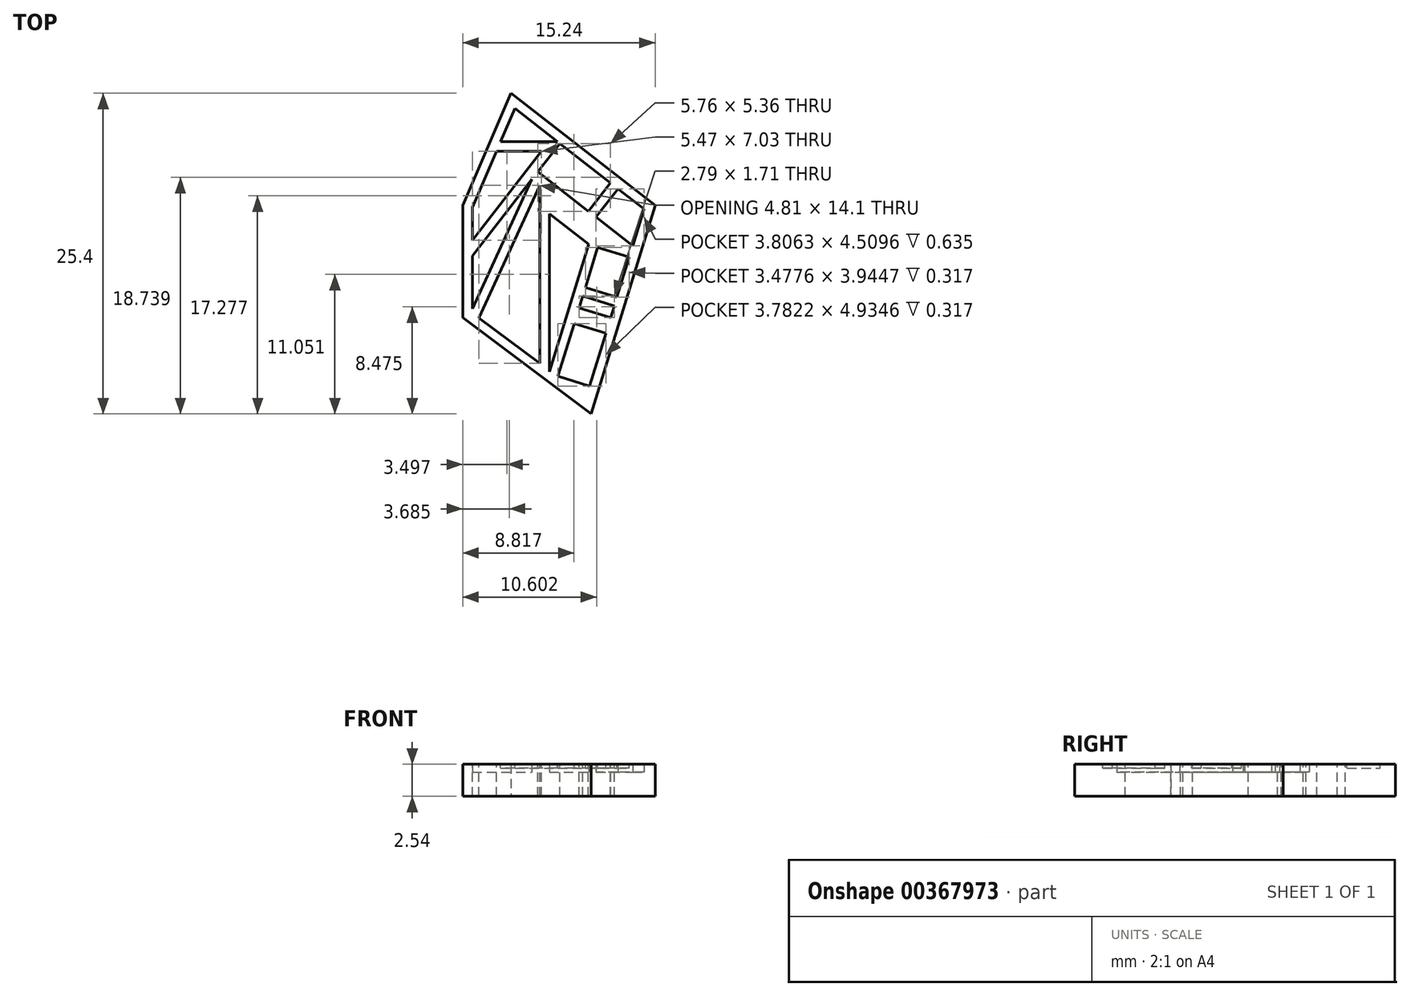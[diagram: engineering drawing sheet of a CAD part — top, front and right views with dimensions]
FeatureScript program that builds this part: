
annotation { "Feature Type Name" : "Feature", "Feature Type Description" : "" }
export const myFeature = defineFeature(function(context is Context, id is Id, definition is map)
    precondition{}
    {
        {
            var Q0;
            Q0=qCreatedBy(makeId("Top.planeOp"),FACE);
            var sketch = newSketch(context, id + "F0", { "sketchPlane" : qUnion([Q0])});
            skLineSegment(sketch, "E0", {"start": v(0, 17.78) * mm, "end": v(11.43, 8.9) * mm});
            skLineSegment(sketch, "E1", {"start": v(11.43, 8.9) * mm, "end": v(6.35, -7.62) * mm});
            skLineSegment(sketch, "E2", {"start": v(6.35, -7.62) * mm, "end": v(-3.81, 0) * mm});
            skLineSegment(sketch, "E3", {"start": v(-3.8, 0) * mm, "end": v(-3.8, 8.9) * mm});
            skLineSegment(sketch, "E4", {"start": v(-3.81, 8.9) * mm, "end": v(0, 17.78) * mm});
            skSolve(sketch);
        }
        {
            var Q0;
            Q0=makeQuery(id+"F0.imprint","IMPRINT",FACE,{"disambiguationData":[TD([[makeQuery(id+"F0.imprint","IMPRINT",EDGE,{"derivedFrom":sQuery(id+"F0.wireOp",EDGE,"E0")}),-1.0]])]});
            extrude(context, id + "F1", {"entities" : qUnion([Q0]), "depth" : 2.54 * mm});
        }
        {
            var Q0;
            Q0=makeQuery(id+"F1.opExtrude","CAP_FACE",FACE,{"disambiguationData":[OSD([sQuery(id+"F0.wireOp",EDGE,"E0"),sQuery(id+"F0.wireOp",EDGE,"E1"),sQuery(id+"F0.wireOp",EDGE,"E2"),sQuery(id+"F0.wireOp",EDGE,"E3"),sQuery(id+"F0.wireOp",EDGE,"E4")])],"isStart":false});
            var sketch = newSketch(context, id + "F2", { "sketchPlane" : qUnion([Q0])});
            skLineSegment(sketch, "E5", {"start": v(0.31, 16.57) * mm, "end": v(-0.82, 13.93) * mm});
            skLineSegment(sketch, "E6", {"start": v(-0.82, 13.93) * mm, "end": v(3.7, 13.93) * mm});
            skLineSegment(sketch, "E7", {"start": v(3.7, 13.93) * mm, "end": v(0.31, 16.57) * mm});
            skLineSegment(sketch, "E8", {"start": v(2.42, 13.17) * mm, "end": v(-1.15, 13.17) * mm});
            skLineSegment(sketch, "E9", {"start": v(-1.15, 13.17) * mm, "end": v(-3.05, 8.73) * mm});
            skLineSegment(sketch, "E10", {"start": v(-3.05, 8.73) * mm, "end": v(-3.05, 6.14) * mm});
            skLineSegment(sketch, "E11", {"start": v(-3.05, 6.14) * mm, "end": v(2.42, 13.17) * mm});
            skLineSegment(sketch, "E12", {"start": v(3.88, 13.8) * mm, "end": v(2.13, 11.56) * mm});
            skLineSegment(sketch, "E13", {"start": v(2.13, 11.56) * mm, "end": v(6.14, 8.44) * mm});
            skLineSegment(sketch, "E14", {"start": v(6.14, 8.44) * mm, "end": v(7.89, 10.68) * mm});
            skLineSegment(sketch, "E15", {"start": v(7.89, 10.68) * mm, "end": v(3.88, 13.8) * mm});
            skLineSegment(sketch, "E16", {"start": v(8.49, 10.21) * mm, "end": v(6.74, 7.97) * mm});
            skLineSegment(sketch, "E17", {"start": v(6.74, 7.97) * mm, "end": v(9.65, 5.7) * mm});
            skLineSegment(sketch, "E18", {"start": v(9.65, 5.7) * mm, "end": v(10.55, 8.61) * mm});
            skLineSegment(sketch, "E19", {"start": v(10.55, 8.61) * mm, "end": v(8.49, 10.21) * mm});
            skLineSegment(sketch, "E20", {"start": v(1.66, 10.95) * mm, "end": v(-3.05, 4.9) * mm});
            skLineSegment(sketch, "E21", {"start": v(-3.05, 4.9) * mm, "end": v(-3.05, 0.7) * mm});
            skLineSegment(sketch, "E22", {"start": v(-3.05, 0.7) * mm, "end": v(1.66, 10.95) * mm});
            skLineSegment(sketch, "E23", {"start": v(2.28, 10.48) * mm, "end": v(2.28, -3.62) * mm});
            skLineSegment(sketch, "E24", {"start": v(2.28, -3.62) * mm, "end": v(-2.53, 0) * mm});
            skLineSegment(sketch, "E25", {"start": v(-2.53, 0) * mm, "end": v(2.28, 10.48) * mm});
            skLineSegment(sketch, "E26", {"start": v(3.04, 8.25) * mm, "end": v(3.04, -4.29) * mm});
            skLineSegment(sketch, "E27", {"start": v(3.04, -4.29) * mm, "end": v(6.16, 5.83) * mm});
            skLineSegment(sketch, "E28", {"start": v(3.04, 8.25) * mm, "end": v(6.16, 5.83) * mm});
            skLineSegment(sketch, "E29", {"start": v(6.88, 5.58) * mm, "end": v(5.9, 2.4) * mm});
            skLineSegment(sketch, "E30", {"start": v(5.9, 2.4) * mm, "end": v(8.4, 1.63) * mm});
            skLineSegment(sketch, "E31", {"start": v(8.4, 1.63) * mm, "end": v(9.38, 4.8) * mm});
            skLineSegment(sketch, "E32", {"start": v(9.38, 4.8) * mm, "end": v(6.88, 5.58) * mm});
            skLineSegment(sketch, "E33", {"start": v(5.69, 1.71) * mm, "end": v(5.4, 0.77) * mm});
            skPoint(sketch, "E33.endSnap0", {"position": v(4.6, 0.77) * mm});
            skLineSegment(sketch, "E34", {"start": v(5.4, 0.77) * mm, "end": v(7.9, 0) * mm});
            skLineSegment(sketch, "E35", {"start": v(7.9, 0) * mm, "end": v(8.19, 0.94) * mm});
            skLineSegment(sketch, "E36", {"start": v(5.69, 1.71) * mm, "end": v(8.19, 0.94) * mm});
            skLineSegment(sketch, "E37", {"start": v(5.02, -0.47) * mm, "end": v(3.73, -4.64) * mm});
            skLineSegment(sketch, "E38", {"start": v(3.73, -4.64) * mm, "end": v(6.23, -5.4) * mm});
            skLineSegment(sketch, "E39", {"start": v(6.23, -5.4) * mm, "end": v(7.52, -1.24) * mm});
            skLineSegment(sketch, "E40", {"start": v(7.52, -1.24) * mm, "end": v(5.02, -0.47) * mm});
            skSolve(sketch);
        }
        {
            var Q0;
            Q0=makeQuery(id+"F2.imprint","IMPRINT",FACE,{"disambiguationData":[TD([[makeQuery(id+"F2.imprint","IMPRINT",EDGE,{"derivedFrom":sQuery(id+"F2.wireOp",EDGE,"E8")}),1.0]])]});
            var Q1;
            Q1=makeQuery(id+"F2.imprint","IMPRINT",FACE,{"disambiguationData":[TD([[makeQuery(id+"F2.imprint","IMPRINT",EDGE,{"derivedFrom":sQuery(id+"F2.wireOp",EDGE,"E12")}),1.0]])]});
            var Q2;
            Q2=makeQuery(id+"F2.imprint","IMPRINT",FACE,{"disambiguationData":[TD([[makeQuery(id+"F2.imprint","IMPRINT",EDGE,{"derivedFrom":sQuery(id+"F2.wireOp",EDGE,"E23")}),-1.0]])]});
            var Q3;
            Q3=makeQuery(id+"F2.imprint","IMPRINT",FACE,{"disambiguationData":[TD([[makeQuery(id+"F2.imprint","IMPRINT",EDGE,{"derivedFrom":sQuery(id+"F2.wireOp",EDGE,"E33")}),1.0]])]});
            extrude(context, id + "F3", {"entities" : qUnion([Q0, Q1, Q2, Q3]), "operationType" : NewBodyOperationType.REMOVE, "endBound" : BoundingType.THROUGH_ALL, "oppositeDirection" : true, "depth" : 25.4 * mm});
        }
        {
            var Q0;
            Q0=makeQuery(id+"F2.imprint","IMPRINT",FACE,{"disambiguationData":[TD([[makeQuery(id+"F2.imprint","IMPRINT",EDGE,{"derivedFrom":sQuery(id+"F2.wireOp",EDGE,"E26")}),1.0]])]});
            var Q1;
            Q1=makeQuery(id+"F2.imprint","IMPRINT",FACE,{"disambiguationData":[TD([[makeQuery(id+"F2.imprint","IMPRINT",EDGE,{"derivedFrom":sQuery(id+"F2.wireOp",EDGE,"E16")}),1.0]])]});
            var Q2;
            Q2=makeQuery(id+"F2.imprint","IMPRINT",FACE,{"disambiguationData":[TD([[makeQuery(id+"F2.imprint","IMPRINT",EDGE,{"derivedFrom":sQuery(id+"F2.wireOp",EDGE,"E20")}),1.0]])]});
            extrude(context, id + "F4", {"entities" : qUnion([Q0, Q1, Q2]), "operationType" : NewBodyOperationType.REMOVE, "endBound" : BoundingType.SYMMETRIC, "depth" : 1.27 * mm});
        }
        {
            var Q0;
            Q0=makeQuery(id+"F2.imprint","IMPRINT",FACE,{"disambiguationData":[TD([[makeQuery(id+"F2.imprint","IMPRINT",EDGE,{"derivedFrom":sQuery(id+"F2.wireOp",EDGE,"E37")}),1.0]])]});
            var Q1;
            Q1=makeQuery(id+"F2.imprint","IMPRINT",FACE,{"disambiguationData":[TD([[makeQuery(id+"F2.imprint","IMPRINT",EDGE,{"derivedFrom":sQuery(id+"F2.wireOp",EDGE,"E29")}),1.0]])]});
            var Q2;
            Q2=makeQuery(id+"F2.imprint","IMPRINT",FACE,{"disambiguationData":[TD([[makeQuery(id+"F2.imprint","IMPRINT",EDGE,{"derivedFrom":sQuery(id+"F2.wireOp",EDGE,"E5")}),1.0]])]});
            extrude(context, id + "F5", {"entities" : qUnion([Q0, Q1, Q2]), "operationType" : NewBodyOperationType.REMOVE, "endBound" : BoundingType.SYMMETRIC, "oppositeDirection" : true, "depth" : 0.64 * mm});
        }
    });
